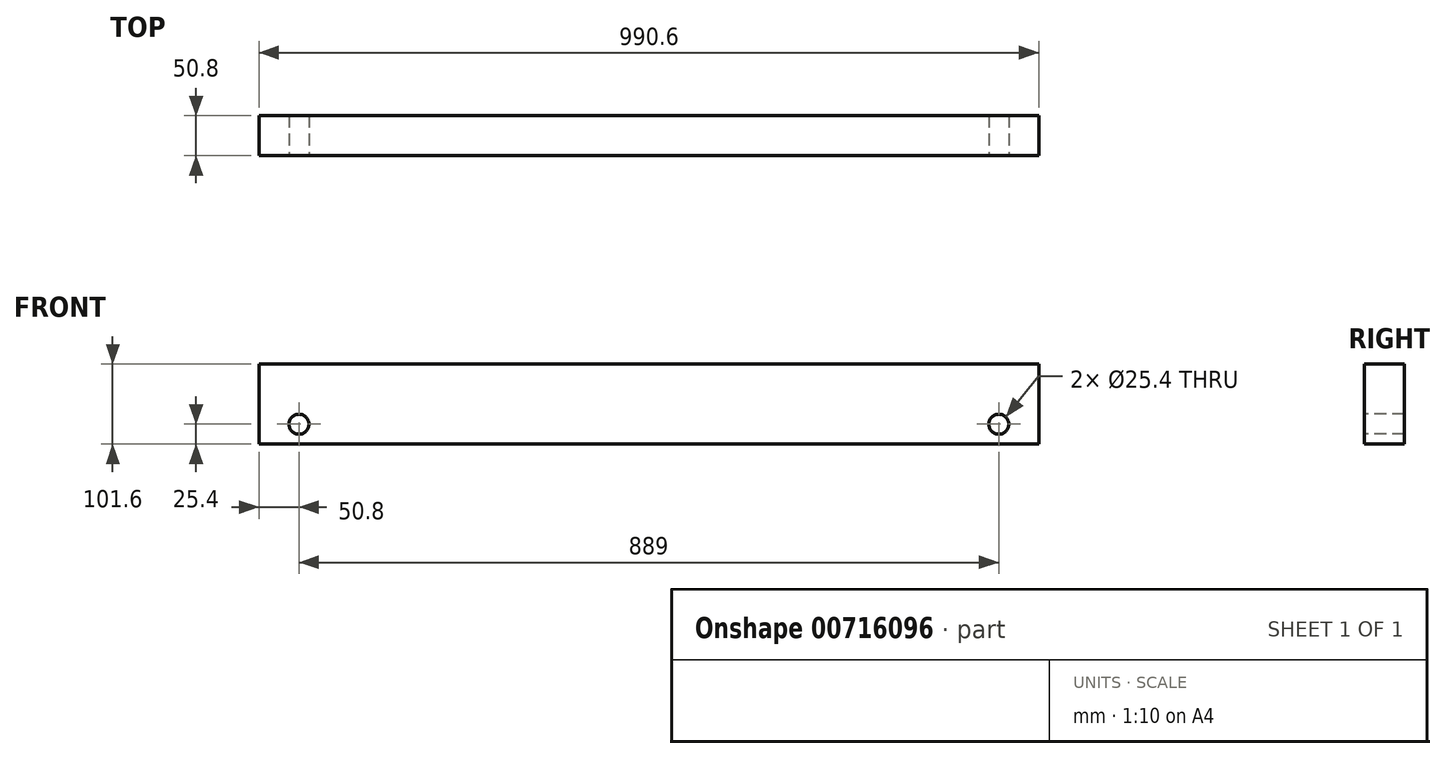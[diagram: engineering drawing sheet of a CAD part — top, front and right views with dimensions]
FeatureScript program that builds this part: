
annotation { "Feature Type Name" : "Feature", "Feature Type Description" : "" }
export const myFeature = defineFeature(function(context is Context, id is Id, definition is map)
    precondition{}
    {
        {
            var Q0;
            Q0=qCreatedBy(makeId("Front.planeOp"),FACE);
            var sketch = newSketch(context, id + "F0", { "sketchPlane" : qUnion([Q0])});
            skLineSegment(sketch, "E0.bottom", {"start": v(0, 101.6) * mm, "end": v(990.6, 101.6) * mm});
            skLineSegment(sketch, "E0.top", {"start": v(0, 0) * mm, "end": v(990.6, 0) * mm});
            skLineSegment(sketch, "E0.left", {"start": v(0, 101.6) * mm, "end": v(0, 0) * mm});
            skLineSegment(sketch, "E0.right", {"start": v(990.6, 101.6) * mm, "end": v(990.6, 0) * mm});
            skSolve(sketch);
        }
        {
            var Q0;
            Q0=makeQuery(id+"F0.imprint","IMPRINT",FACE,{"disambiguationData":[TD([[makeQuery(id+"F0.imprint","IMPRINT",EDGE,{"derivedFrom":sQuery(id+"F0.wireOp",EDGE,"E0.bottom")}),-1.0]])]});
            extrude(context, id + "F1", {"entities" : qUnion([Q0]), "depth" : 50.8 * mm, "offsetDistance" : 25.4 * mm});
        }
        {
            var Q0;
            Q0=makeQuery(id+"F1.opExtrude","CAP_FACE",FACE,{"disambiguationData":[OSD([sQuery(id+"F0.wireOp",EDGE,"E0.bottom"),sQuery(id+"F0.wireOp",EDGE,"E0.top"),sQuery(id+"F0.wireOp",EDGE,"E0.left"),sQuery(id+"F0.wireOp",EDGE,"E0.right")])],"isStart":false});
            var sketch = newSketch(context, id + "F2", { "sketchPlane" : qUnion([Q0])});
            skLineSegment(sketch, "E1", {"start": v(0, 50.8) * mm, "end": v(50.8, 50.8) * mm, "construction": true});
            skLineSegment(sketch, "E2", {"start": v(990.6, 50.8) * mm, "end": v(939.8, 50.8) * mm, "construction": true});
            skLineSegment(sketch, "E3", {"start": v(50.8, 101.6) * mm, "end": v(50.8, 50.8) * mm});
            skLineSegment(sketch, "E4", {"start": v(50.8, 50.8) * mm, "end": v(50.8, 0) * mm});
            skPoint(sketch, "E5", {"position": v(50.8, 25.4) * mm});
            skPoint(sketch, "E6", {"position": v(50.8, 76.2) * mm});
            skCircle(sketch, "E7", {"center": v(50.8, 25.4) * mm, "radius": 12.7 * mm});
            skLineSegment(sketch, "E8", {"start": v(939.8, 101.6) * mm, "end": v(939.8, 50.8) * mm});
            skLineSegment(sketch, "E9", {"start": v(939.8, 50.8) * mm, "end": v(939.8, 0) * mm});
            skPoint(sketch, "E10", {"position": v(939.8, 25.4) * mm});
            skPoint(sketch, "E11", {"position": v(939.8, 76.2) * mm});
            skCircle(sketch, "E12", {"center": v(939.8, 25.4) * mm, "radius": 12.7 * mm});
            skSolve(sketch);
        }
        {
            var Q0;
            Q0=qSketchRegion(id+"F2",true);
            extrude(context, id + "F3", {"entities" : qUnion([Q0]), "operationType" : NewBodyOperationType.REMOVE, "endBound" : BoundingType.THROUGH_ALL, "oppositeDirection" : true, "depth" : 25.4 * mm, "offsetDistance" : 25.4 * mm});
        }
    });
